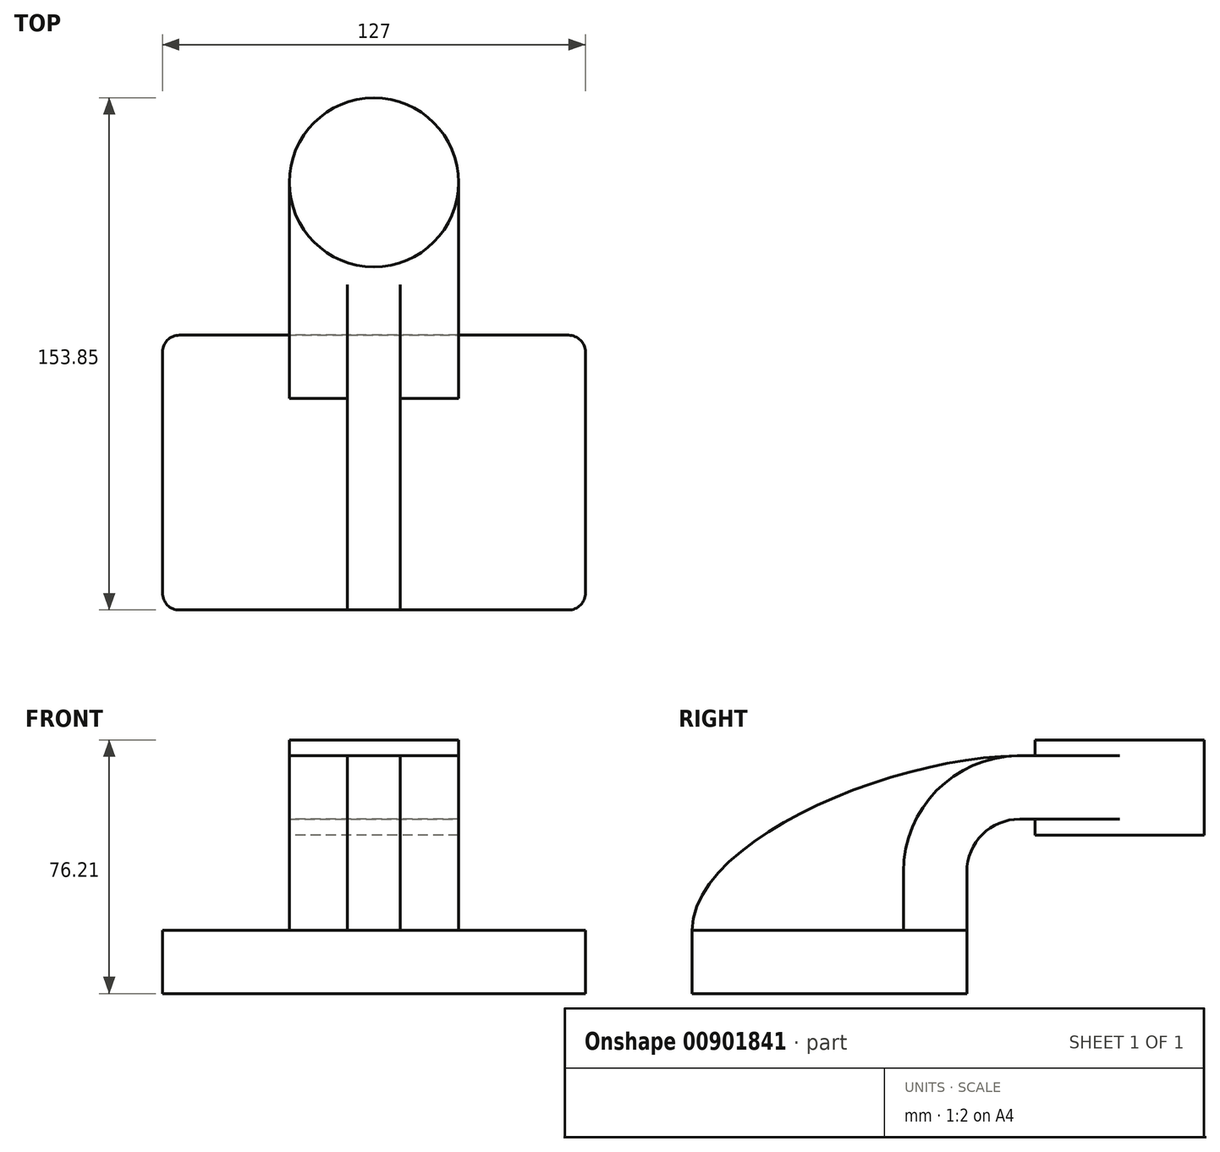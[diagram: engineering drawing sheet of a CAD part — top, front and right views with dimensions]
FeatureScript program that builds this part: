
annotation { "Feature Type Name" : "Feature", "Feature Type Description" : "" }
export const myFeature = defineFeature(function(context is Context, id is Id, definition is map)
    precondition{}
    {
        {
            var Q0;
            Q0=qCreatedBy(makeId("Right.planeOp"),FACE);
            var sketch = newSketch(context, id + "F0", { "sketchPlane" : qUnion([Q0])});
            skLineSegment(sketch, "E0.bottom", {"start": v(-41.28, 9.52) * mm, "end": v(41.27, 9.53) * mm});
            skLineSegment(sketch, "E0.top", {"start": v(-41.28, -9.53) * mm, "end": v(41.28, -9.53) * mm});
            skLineSegment(sketch, "E0.left", {"start": v(-41.28, 9.52) * mm, "end": v(-41.27, -9.53) * mm});
            skLineSegment(sketch, "E0.right", {"start": v(41.28, 9.53) * mm, "end": v(41.28, -9.52) * mm});
            skPoint(sketch, "E0.middle", {"position": v(0, 0) * mm});
            skLineSegment(sketch, "E1.bottom", {"start": v(61.77, 38.1) * mm, "end": v(112.57, 38.1) * mm});
            skLineSegment(sketch, "E1.top", {"start": v(61.77, 66.67) * mm, "end": v(112.57, 66.67) * mm});
            skLineSegment(sketch, "E1.left", {"start": v(61.77, 38.1) * mm, "end": v(61.77, 66.67) * mm});
            skLineSegment(sketch, "E1.right", {"start": v(112.57, 38.1) * mm, "end": v(112.57, 66.67) * mm});
            skPoint(sketch, "E1.middle", {"position": v(87.17, 52.39) * mm});
            skLineSegment(sketch, "E2", {"start": v(41.27, 9.53) * mm, "end": v(41.27, 27) * mm});
            skArc(sketch, "E3", {"start": v(41.27, 27) * mm, "mid": v(45.92, 38.23) * mm, "end": v(57.15, 42.88) * mm});
            skLineSegment(sketch, "E4", {"start": v(57.15, 42.88) * mm, "end": v(87.17, 42.88) * mm});
            skLineSegment(sketch, "E5.0", {"start": v(57.15, 61.93) * mm, "end": v(87.17, 61.93) * mm});
            skArc(sketch, "E5.1", {"start": v(22.22, 27) * mm, "mid": v(32.45, 51.7) * mm, "end": v(57.15, 61.93) * mm});
            skLineSegment(sketch, "E5.2", {"start": v(22.23, 9.53) * mm, "end": v(22.23, 27) * mm});
            skLineSegment(sketch, "E6", {"start": v(87.17, 66.67) * mm, "end": v(87.17, 38.1) * mm});
            skFitSpline(sketch, "E7", {"points": [v(-41.28, 9.52) * mm, v(57.15, 61.93) * mm], "startDerivative": vector(2, 82.77) * mm, "endDerivative": vector(112.12, 0.65) * mm});
            skSolve(sketch);
        }
        {
            var Q0;
            Q0=makeQuery(id+"F0.imprint","IMPRINT",FACE,{"disambiguationData":[TD([[makeQuery(id+"F0.imprint","IMPRINT",EDGE,{"derivedFrom":sQuery(id+"F0.wireOp",EDGE,"E0.top")}),1.0]])]});
            extrude(context, id + "F1", {"entities" : qUnion([Q0]), "endBound" : BoundingType.SYMMETRIC, "oppositeDirection" : true, "depth" : 127 * mm, "offsetDistance" : 25.4 * mm});
        }
        {
            var Q0;
            {var subQ1=sQuery(id+"F0.wireOp",EDGE,"E2");Q0=makeQuery(id+"F0.imprint","IMPRINT",FACE,{"disambiguationData":[TD([[makeQuery(id+"F0.imprint","IMPRINT",EDGE,{"derivedFrom":subQ1}),1.0]])]});}
            extrude(context, id + "F2", {"entities" : qUnion([Q0]), "operationType" : NewBodyOperationType.ADD, "endBound" : BoundingType.SYMMETRIC, "depth" : 50.8 * mm, "offsetDistance" : 25.4 * mm});
        }
        {
            var Q0;
            {var subQ3=sQuery(id+"F0.wireOp",EDGE,"E5.2");Q0=makeQuery(id+"F0.imprint","IMPRINT",FACE,{"disambiguationData":[TD([[makeQuery(id+"F0.imprint","IMPRINT",EDGE,{"derivedFrom":subQ3}),1.0]])]});}
            extrude(context, id + "F3", {"entities" : qUnion([Q0]), "operationType" : NewBodyOperationType.ADD, "endBound" : BoundingType.SYMMETRIC, "depth" : 15.88 * mm, "offsetDistance" : 25.4 * mm});
        }
        {
            var Q0;
            {var subQ0=sQuery(id+"F0.wireOp",EDGE,"E4");var subQ1=sQuery(id+"F0.wireOp",EDGE,"E1.left");var subQ2=makeQuery(id+"F0.imprint","INTERSECT",VERTEX,{"derivedFrom":[subQ1,subQ0]});Q0=makeQuery(id+"F0.imprint","IMPRINT",FACE,{"disambiguationData":[TD([[makeQuery(id+"F0.imprint","IMPRINT",EDGE,{"disambiguationData":[TD([[subQ2,-1.0]])],"derivedFrom":subQ1}),-1.0]])]});}
            extrude(context, id + "F4", {"entities" : qUnion([Q0]), "operationType" : NewBodyOperationType.ADD, "endBound" : BoundingType.SYMMETRIC, "depth" : 50.8 * mm, "offsetDistance" : 25.4 * mm});
        }
        {
            var Q0;
            {var subQ4=sQuery(id+"F0.wireOp",EDGE,"E1.right");Q0=makeQuery(id+"F0.imprint","IMPRINT",FACE,{"disambiguationData":[TD([[makeQuery(id+"F0.imprint","IMPRINT",EDGE,{"derivedFrom":subQ4}),1.0]])]});}
            var Q1;
            Q1=sQuery(id+"F0.wireOp",EDGE,"E6");
            revolve(context, id + "F5", {"operationType" : NewBodyOperationType.ADD, "surfaceOperationType" : NewSurfaceOperationType.NEW, "entities" : qUnion([Q0]), "axis" : qUnion([Q1]), "revolveType" : RevolveType.FULL});
        }
        {
            var Q0;
            Q0=makeQuery(id+"F1.opExtrude","CAP_EDGE",EDGE,{"disambiguationData":[OSD([sQuery(id+"F0.wireOp",EDGE,"E0.left")])],"isStart":true});
            var Q1;
            Q1=makeQuery(id+"F1.opExtrude","CAP_EDGE",EDGE,{"disambiguationData":[OSD([sQuery(id+"F0.wireOp",EDGE,"E0.right")])],"isStart":true});
            var Q2;
            Q2=makeQuery(id+"F1.opExtrude","CAP_EDGE",EDGE,{"disambiguationData":[OSD([sQuery(id+"F0.wireOp",EDGE,"E0.right")])],"isStart":false});
            var Q3;
            Q3=makeQuery(id+"F1.opExtrude","CAP_EDGE",EDGE,{"disambiguationData":[OSD([sQuery(id+"F0.wireOp",EDGE,"E0.left")])],"isStart":false});
            fillet(context, id + "F6", {"entities" : qUnion([Q0, Q1, Q2, Q3]), "radius" : 5.08 * mm, "tangentPropagation" : true, "allowEdgeOverflow" : false});
        }
    });
